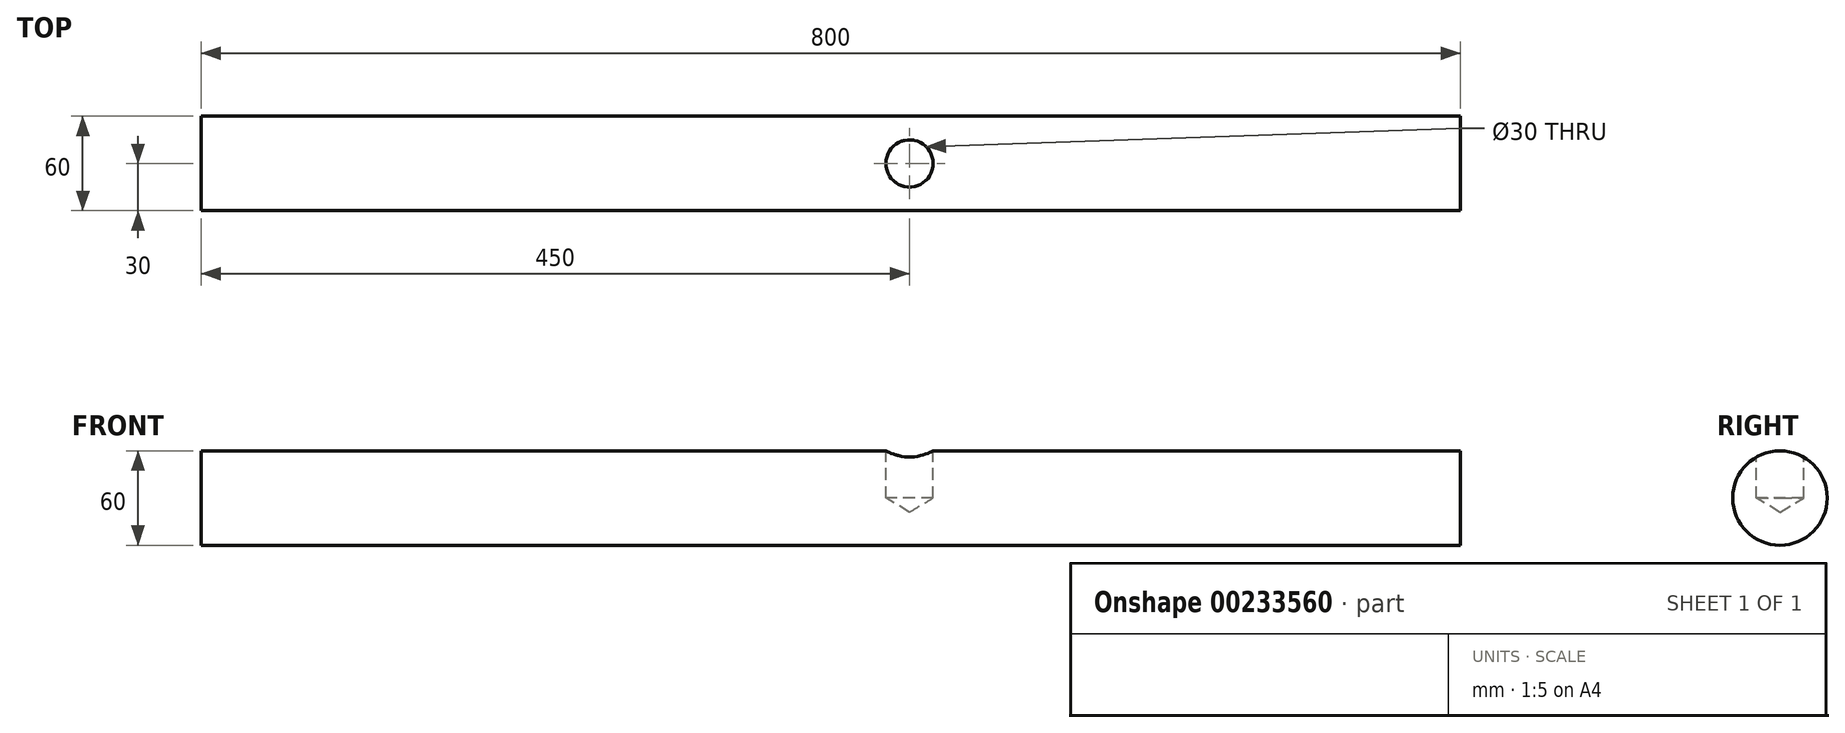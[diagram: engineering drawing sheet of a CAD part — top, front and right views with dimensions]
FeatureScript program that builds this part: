
annotation { "Feature Type Name" : "Feature", "Feature Type Description" : "" }
export const myFeature = defineFeature(function(context is Context, id is Id, definition is map)
    precondition{}
    {
        {
            var Q0;
            Q0=qCreatedBy(makeId("Front.planeOp"),FACE);
            var sketch = newSketch(context, id + "F0", { "sketchPlane" : qUnion([Q0])});
            skLineSegment(sketch, "E0.bottom", {"start": v(400, 30) * mm, "end": v(-400, 30) * mm});
            skLineSegment(sketch, "E0.left", {"start": v(400, 30) * mm, "end": v(400, 0) * mm});
            skLineSegment(sketch, "E0.right", {"start": v(-400, 30) * mm, "end": v(-400, 0) * mm});
            skPoint(sketch, "E0.middle", {"position": v(0, 0) * mm});
            skLineSegment(sketch, "E1", {"start": v(-300, 30) * mm, "end": v(-300, 0) * mm});
            skLineSegment(sketch, "E2", {"start": v(-400, 0) * mm, "end": v(400, 0) * mm});
            skPoint(sketch, "E2.startSnap0", {"position": v(-400, 0) * mm});
            skPoint(sketch, "E3.orphan", {"position": v(-400, -30) * mm});
            skPoint(sketch, "E4.orphan", {"position": v(400, -30) * mm});
            skSolve(sketch);
        }
        {
            var Q0;
            {var subQ0=sQuery(id+"F0.wireOp",EDGE,"E0.left");Q0=makeQuery(id+"F0.imprint","IMPRINT",FACE,{"disambiguationData":[TD([[makeQuery(id+"F0.imprint","IMPRINT",EDGE,{"derivedFrom":subQ0}),-1.0]])]});}
            var Q1;
            {var subQ0=sQuery(id+"F0.wireOp",EDGE,"E0.right");Q1=makeQuery(id+"F0.imprint","IMPRINT",FACE,{"disambiguationData":[TD([[makeQuery(id+"F0.imprint","IMPRINT",EDGE,{"derivedFrom":subQ0}),1.0]])]});}
            var Q2;
            Q2=sQuery(id+"F0.wireOp",EDGE,"E2");
            revolve(context, id + "F1", {"entities" : qUnion([Q0, Q1]), "axis" : qUnion([Q2]), "revolveType" : RevolveType.FULL});
        }
        {
            var Q0;
            Q0=qCreatedBy(makeId("Top.planeOp"),FACE);
            cPlane(context, id + "F2", {"entities" : qUnion([Q0]), "cplaneType" : CPlaneType.OFFSET, "offset" : 30 * mm, "width" : 150 * mm, "height" : 150 * mm});
        }
        {
            var Q0;
            Q0=qCreatedBy(id+"F2.planeOp",FACE);
            var sketch = newSketch(context, id + "F3", { "sketchPlane" : qUnion([Q0])});
            skCircle(sketch, "E5", {"center": v(50, 0) * mm, "radius": 15 * mm, "construction": true});
            skSolve(sketch);
        }
        {
            var Q0;
            Q0=sQuery(id+"F3.wireOp",VERTEX,"E5.center");
            var Q1;
            Q1=makeQuery(id+"F1.opRevolve","SWEPT_BODY",BODY,{"disambiguationData":[OSD([sQuery(id+"F0.wireOp",EDGE,"E0.bottom"),sQuery(id+"F0.wireOp",EDGE,"E0.left"),sQuery(id+"F0.wireOp",EDGE,"E0.right"),sQuery(id+"F0.wireOp",EDGE,"E2")])]});
            hole(context, id + "F4", {"style" : HoleStyle.SIMPLE, "endStyle" : HoleEndStyle.BLIND, "holeDiameter" : 30 * mm, "holeDepth" : 30 * mm, "startFromSketch" : true, "locations" : qUnion([Q0]), "scope" : qUnion([Q1])});
        }
    });
